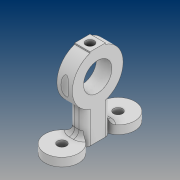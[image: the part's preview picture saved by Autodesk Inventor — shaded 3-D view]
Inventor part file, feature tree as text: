
AUTODESK INVENTOR PART (.ipt)
format: ipt  version: 2021 (Build 250183000, 183)  size: 199,168 bytes
history: native  units: mm
features: sketch x5, extrude x4, projected_geometry x2, hole x1, fillet x1, plane x1
ambient origin geometry x8: Origin, YZ Plane, XZ Plane, XY Plane, X Axis, Y Axis, Z Axis, Center Point
bodies: Solid1 (feature_tree)
feature tree (14):
  extrude  "Extrusion1"  Depth=12.0mm
  extrude  "Extrusion2"  Depth=5.5mm TaperAngle=0.0deg
  hole  "Hole1"  [1 undecoded]
  fillet  "Fillet1"  Radius=4.0mm
  plane  "Work Plane1"
  extrude  "Extrusion3"  Depth=5.5mm
  extrude  "Extrusion4"  Depth=5.5mm
  sketch  "Sketch1"  dims[d0=20.0mm d1=12.0mm]
  sketch  "Sketch2"  dims[d2=5.5mm d3=3.0mm d4=0.0mm]
  projected_geometry  "Projected Loop1"
  sketch  "Sketch3"  dims[d5=10.1mm d6=20.0mm d7=4.0mm]
  projected_geometry  "Projected Loop2"
  sketch  "Sketch4"  dims[d9=5.5mm d10=0.0mm]
  sketch  "Sketch5"  dims[d11=3.2mm d12=6.0mm d13=4.0mm d14=2.0mm d15=90.0deg d16=8.0mm d17=20.594885mm d18=2.0mm d19=5.5mm d21=2.0mm d22=0.0mm d23=3.0mm d24=7.75mm d25=0.0mm]
note: 1 required parameter value undecoded (feature->parameter linkage not recoverable at this tier; creation-order binding heuristic only, values carry confidence <= 0.55)
